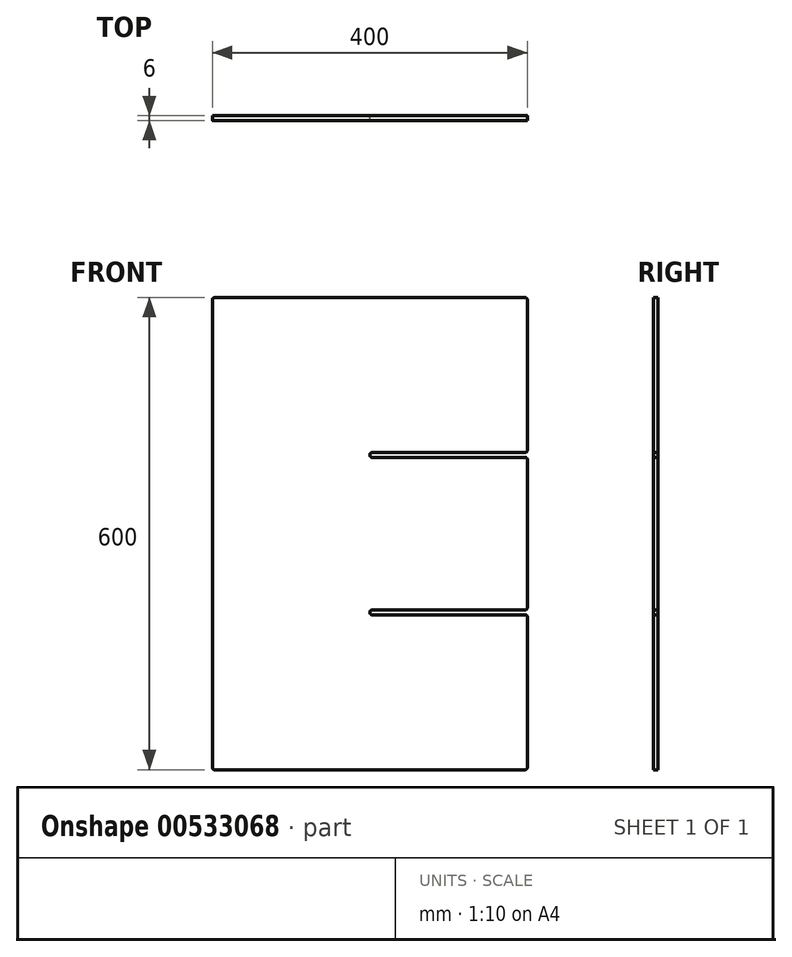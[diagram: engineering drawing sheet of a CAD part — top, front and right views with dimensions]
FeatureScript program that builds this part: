
annotation { "Feature Type Name" : "Feature", "Feature Type Description" : "" }
export const myFeature = defineFeature(function(context is Context, id is Id, definition is map)
    precondition{}
    {
        {
            var Q0;
            Q0=qCreatedBy(makeId("Front.planeOp"),FACE);
            var sketch = newSketch(context, id + "F0", { "sketchPlane" : qUnion([Q0])});
            skLineSegment(sketch, "E0.bottom", {"start": v(-503.66, 330.59) * mm, "end": v(-109.66, 330.59) * mm});
            skLineSegment(sketch, "E0.top", {"start": v(-503.66, -269.41) * mm, "end": v(-109.66, -269.41) * mm});
            skLineSegment(sketch, "E0.left", {"start": v(-506.66, 327.59) * mm, "end": v(-506.66, -266.41) * mm});
            skLineSegment(sketch, "E0.right", {"start": v(-106.66, 327.59) * mm, "end": v(-106.66, 136.59) * mm});
            skLineSegment(sketch, "E1.bottom", {"start": v(-109.66, 127.59) * mm, "end": v(-303.66, 127.59) * mm});
            skLineSegment(sketch, "E1.top", {"start": v(-109.66, 133.59) * mm, "end": v(-303.66, 133.59) * mm});
            skLineSegment(sketch, "E1.right", {"start": v(-306.66, 130.59) * mm, "end": v(-306.66, 130.59) * mm});
            skLineSegment(sketch, "E2.bottom", {"start": v(-109.66, -72.41) * mm, "end": v(-303.66, -72.41) * mm});
            skLineSegment(sketch, "E2.top", {"start": v(-109.66, -66.41) * mm, "end": v(-303.66, -66.41) * mm});
            skLineSegment(sketch, "E2.right", {"start": v(-306.66, -69.41) * mm, "end": v(-306.66, -69.41) * mm});
            skLineSegment(sketch, "E3.trimOffspring", {"start": v(-106.66, 124.59) * mm, "end": v(-106.66, -63.41) * mm});
            skLineSegment(sketch, "E4.trimOffspring", {"start": v(-106.66, -75.41) * mm, "end": v(-106.66, -266.41) * mm});
            skPoint(sketch, "E5.visualSharp", {"position": v(-306.66, -66.41) * mm});
            skArc(sketch, "E5.filletArc", {"start": v(-303.66, -66.41) * mm, "mid": v(-305.79, -67.3) * mm, "end": v(-306.66, -69.41) * mm});
            skPoint(sketch, "E6.visualSharp", {"position": v(-306.66, -72.41) * mm});
            skArc(sketch, "E6.filletArc", {"start": v(-306.66, -69.41) * mm, "mid": v(-305.79, -71.53) * mm, "end": v(-303.66, -72.41) * mm});
            skPoint(sketch, "E7.visualSharp", {"position": v(-306.66, 133.59) * mm});
            skArc(sketch, "E7.filletArc", {"start": v(-303.66, 133.59) * mm, "mid": v(-305.79, 132.7) * mm, "end": v(-306.66, 130.59) * mm});
            skPoint(sketch, "E8.visualSharp", {"position": v(-306.66, 127.59) * mm});
            skArc(sketch, "E8.filletArc", {"start": v(-306.66, 130.59) * mm, "mid": v(-305.79, 128.47) * mm, "end": v(-303.66, 127.59) * mm});
            skPoint(sketch, "E9.visualSharp", {"position": v(-106.66, 330.59) * mm});
            skArc(sketch, "E9.filletArc", {"start": v(-106.66, 327.59) * mm, "mid": v(-107.54, 329.7) * mm, "end": v(-109.66, 330.59) * mm});
            skPoint(sketch, "E10.visualSharp", {"position": v(-506.66, 330.59) * mm});
            skArc(sketch, "E10.filletArc", {"start": v(-503.66, 330.59) * mm, "mid": v(-505.79, 329.7) * mm, "end": v(-506.66, 327.59) * mm});
            skPoint(sketch, "E11.visualSharp", {"position": v(-506.66, -269.41) * mm});
            skArc(sketch, "E11.filletArc", {"start": v(-506.66, -266.41) * mm, "mid": v(-505.79, -268.53) * mm, "end": v(-503.66, -269.41) * mm});
            skPoint(sketch, "E12.visualSharp", {"position": v(-106.66, -269.41) * mm});
            skArc(sketch, "E12.filletArc", {"start": v(-109.66, -269.41) * mm, "mid": v(-107.54, -268.53) * mm, "end": v(-106.66, -266.41) * mm});
            skPoint(sketch, "E13.visualSharp", {"position": v(-106.66, -72.41) * mm});
            skArc(sketch, "E13.filletArc", {"start": v(-106.66, -75.41) * mm, "mid": v(-107.54, -73.3) * mm, "end": v(-109.66, -72.41) * mm});
            skPoint(sketch, "E14.visualSharp", {"position": v(-106.66, -66.41) * mm});
            skArc(sketch, "E14.filletArc", {"start": v(-109.66, -66.41) * mm, "mid": v(-107.54, -65.53) * mm, "end": v(-106.66, -63.41) * mm});
            skPoint(sketch, "E15.visualSharp", {"position": v(-106.66, 127.59) * mm});
            skArc(sketch, "E15.filletArc", {"start": v(-106.66, 124.59) * mm, "mid": v(-107.54, 126.7) * mm, "end": v(-109.66, 127.59) * mm});
            skPoint(sketch, "E16.visualSharp", {"position": v(-106.66, 133.59) * mm});
            skArc(sketch, "E16.filletArc", {"start": v(-109.66, 133.59) * mm, "mid": v(-107.54, 134.47) * mm, "end": v(-106.66, 136.59) * mm});
            skSolve(sketch);
        }
        {
            var Q0;
            Q0=makeQuery(id+"F0.imprint","IMPRINT",FACE,{"disambiguationData":[TD([[makeQuery(id+"F0.imprint","IMPRINT",EDGE,{"derivedFrom":sQuery(id+"F0.wireOp",EDGE,"E0.bottom")}),-1.0]])]});
            extrude(context, id + "F1", {"entities" : qUnion([Q0]), "depth" : 6 * mm, "offsetDistance" : 25 * mm});
        }
    });
